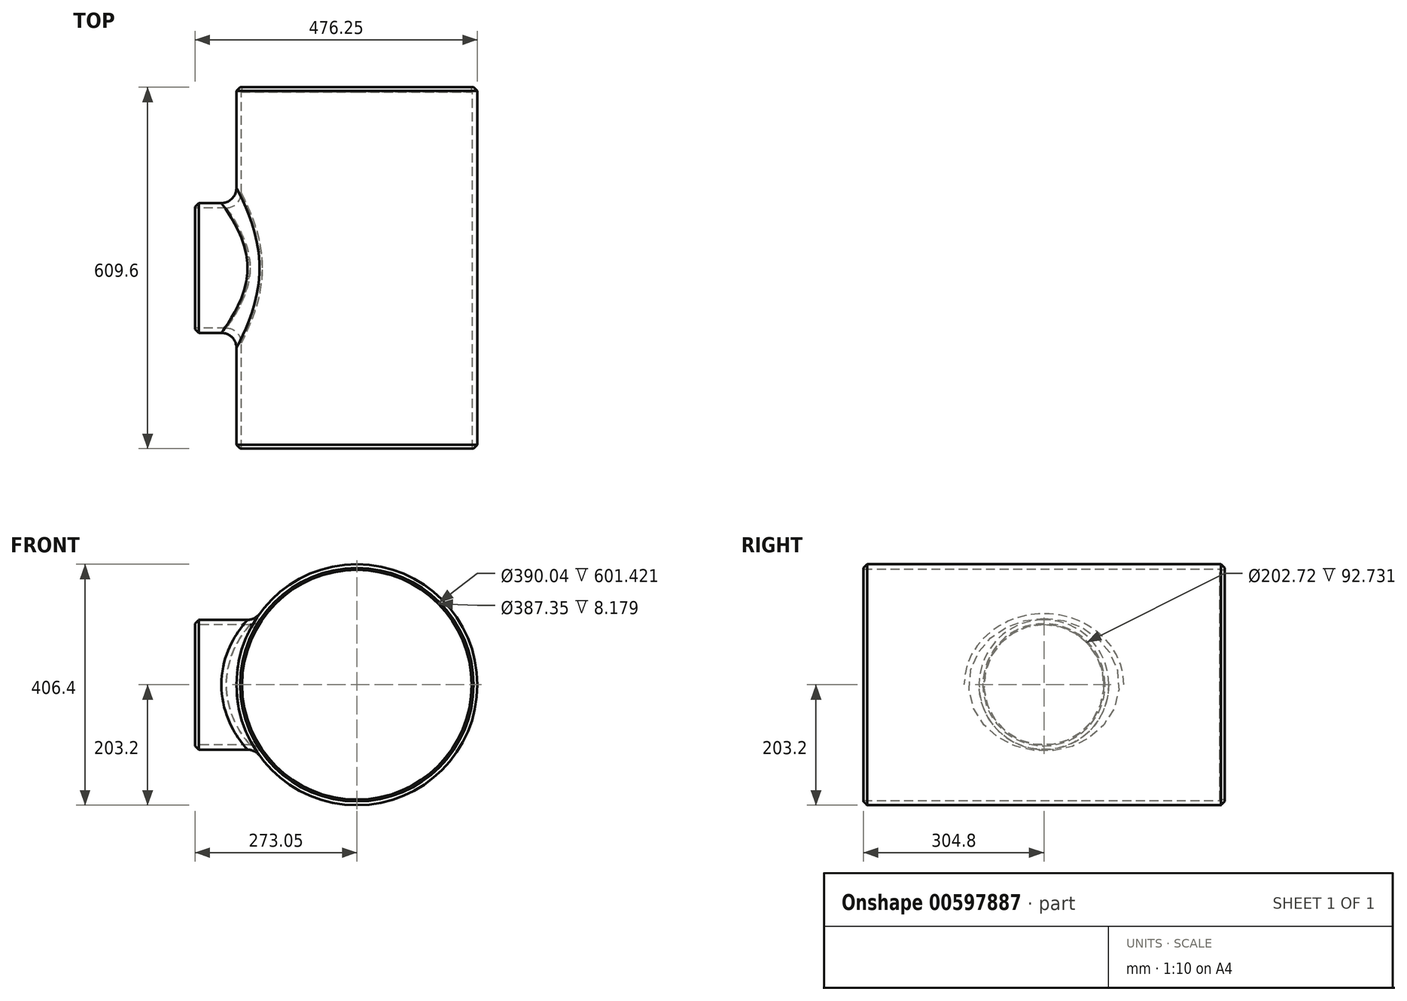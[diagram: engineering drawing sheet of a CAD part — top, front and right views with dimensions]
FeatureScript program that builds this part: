
annotation { "Feature Type Name" : "Feature", "Feature Type Description" : "" }
export const myFeature = defineFeature(function(context is Context, id is Id, definition is map)
    precondition{}
    {
        {
            var Q0;
            Q0=qCreatedBy(makeId("Top.planeOp"),FACE);
            var sketch = newSketch(context, id + "F0", { "sketchPlane" : qUnion([Q0])});
            skLineSegment(sketch, "E0.bottom", {"start": v(203.2, 304.8) * mm, "end": v(-203.2, 304.8) * mm});
            skLineSegment(sketch, "E0.top", {"start": v(203.2, -304.8) * mm, "end": v(-203.2, -304.8) * mm});
            skLineSegment(sketch, "E0.left", {"start": v(203.2, 304.8) * mm, "end": v(203.2, -304.8) * mm});
            skLineSegment(sketch, "E0.right", {"start": v(-203.2, 304.8) * mm, "end": v(-203.2, -304.8) * mm});
            skPoint(sketch, "E0.middle", {"position": v(0, 0) * mm});
            skSolve(sketch);
        }
        {
            var Q0;
            Q0 = qSketchRegion(id + "F0", true);
            extrude(context, id + "F1", {"entities" : qUnion([Q0]), "depth" : 406.4 * mm, "offsetDistance" : 25.4 * mm});
        }
        {
            var Q0;
            Q0=makeQuery(id+"F1.opExtrude","SWEPT_FACE",FACE,{"disambiguationData":[OSD([sQuery(id+"F0.wireOp",EDGE,"E0.right")])]});
            var sketch = newSketch(context, id + "F2", { "sketchPlane" : qUnion([Q0])});
            skCircle(sketch, "E1", {"center": v(0, 203.2) * mm, "radius": 109.47 * mm});
            skPoint(sketch, "E1.centerSnap0", {"position": v(304.8, 203.2) * mm});
            skSolve(sketch);
        }
        {
            var Q0;
            Q0 = qSketchRegion(id + "F2", true);
            extrude(context, id + "F3", {"entities" : qUnion([Q0]), "operationType" : NewBodyOperationType.ADD, "depth" : 69.85 * mm, "offsetDistance" : 25.4 * mm});
        }
        {
            var Q0;
            Q0=makeQuery(id+"F1.opExtrude","CAP_EDGE",EDGE,{"disambiguationData":[OSD([sQuery(id+"F0.wireOp",EDGE,"E0.left")])],"isStart":false});
            var Q1;
            Q1=makeQuery(id+"F1.opExtrude","CAP_EDGE",EDGE,{"disambiguationData":[OSD([sQuery(id+"F0.wireOp",EDGE,"E0.right")])],"isStart":false});
            var Q2;
            Q2=makeQuery(id+"F1.opExtrude","CAP_EDGE",EDGE,{"disambiguationData":[OSD([sQuery(id+"F0.wireOp",EDGE,"E0.right")])],"isStart":true});
            var Q3;
            Q3=makeQuery(id+"F1.opExtrude","CAP_EDGE",EDGE,{"disambiguationData":[OSD([sQuery(id+"F0.wireOp",EDGE,"E0.left")])],"isStart":true});
            fillet(context, id + "F4", {"entities" : qUnion([Q0, Q1, Q2, Q3]), "radius" : 203.2 * mm, "tangentPropagation" : true, "allowEdgeOverflow" : false});
        }
        {
            var Q0;
            Q0=makeQuery(id+"F1.opExtrude","SWEPT_FACE",FACE,{"disambiguationData":[OSD([sQuery(id+"F0.wireOp",EDGE,"E0.top")])]});
            shell(context, id + "F5", {"entities" : qUnion([Q0]), "thickness" : 8.18 * mm});
        }
        {
            var Q0;
            Q0=makeQuery(id+"F3.opExtrude","CAP_FACE",FACE,{"disambiguationData":[OSD([sQuery(id+"F2.wireOp",EDGE,"E1")])],"isStart":false});
            var sketch = newSketch(context, id + "F6", { "sketchPlane" : qUnion([Q0])});
            skCircle(sketch, "E2", {"center": v(0, 203.2) * mm, "radius": 101.36 * mm});
            skSolve(sketch);
        }
        {
            var Q0;
            Q0 = qSketchRegion(id + "F6", true);
            extrude(context, id + "F7", {"entities" : qUnion([Q0]), "operationType" : NewBodyOperationType.REMOVE, "oppositeDirection" : true, "depth" : 203.2 * mm, "offsetDistance" : 25.4 * mm});
        }
        {
            var Q0;
            Q0=makeQuery(id+"F4.opFillet","BLEND_EDGE",EDGE,{"blendedFrom":[makeQuery(id+"F1.opExtrude","CAP_EDGE",EDGE,{"disambiguationData":[OSD([sQuery(id+"F0.wireOp",EDGE,"E0.right")])],"isStart":false}),makeQuery(id+"F3.opExtrude","SWEPT_FACE",FACE,{"disambiguationData":[OSD([sQuery(id+"F2.wireOp",EDGE,"E1")])]})],"blendedInto":[makeQuery(id+"F3.opExtrude","SWEPT_FACE",FACE,{"disambiguationData":[OSD([sQuery(id+"F2.wireOp",EDGE,"E1")])]})]});
            var Q1;
            Q1=makeQuery(id+"F7.boolean.opBoolean","INTERSECT",EDGE,{"derivedFrom":[makeQuery(id+"F5.opShell","OFFSET_FACE",FACE,{"disambiguationData":[OSD([sQuery(id+"F0.wireOp",EDGE,"E0.left")])]}),makeQuery(id+"F7.opExtrude","SWEPT_FACE",FACE,{"disambiguationData":[OSD([sQuery(id+"F6.wireOp",EDGE,"E2")])]})]});
            fillet(context, id + "F8", {"entities" : qUnion([Q0, Q1]), "radius" : 25.4 * mm, "tangentPropagation" : true, "allowEdgeOverflow" : false});
        }
        {
            var Q0;
            Q0=makeQuery(id+"F4.opFillet","BLEND_EDGE",EDGE,{"blendedFrom":[makeQuery(id+"F1.opExtrude","CAP_EDGE",EDGE,{"disambiguationData":[OSD([sQuery(id+"F0.wireOp",EDGE,"E0.left")])],"isStart":true}),makeQuery(id+"F1.opExtrude","SWEPT_FACE",FACE,{"disambiguationData":[OSD([sQuery(id+"F0.wireOp",EDGE,"E0.top")])]})],"blendedInto":[makeQuery(id+"F1.opExtrude","SWEPT_FACE",FACE,{"disambiguationData":[OSD([sQuery(id+"F0.wireOp",EDGE,"E0.top")])]})]});
            var Q1;
            Q1=makeQuery(id+"F4.opFillet","BLEND_EDGE",EDGE,{"blendedFrom":[makeQuery(id+"F1.opExtrude","CAP_EDGE",EDGE,{"disambiguationData":[OSD([sQuery(id+"F0.wireOp",EDGE,"E0.left")])],"isStart":true}),makeQuery(id+"F1.opExtrude","SWEPT_FACE",FACE,{"disambiguationData":[OSD([sQuery(id+"F0.wireOp",EDGE,"E0.bottom")])]})],"blendedInto":[makeQuery(id+"F1.opExtrude","SWEPT_FACE",FACE,{"disambiguationData":[OSD([sQuery(id+"F0.wireOp",EDGE,"E0.bottom")])]})]});
            var Q2;
            Q2=makeQuery(id+"F3.opExtrude","CAP_EDGE",EDGE,{"disambiguationData":[OSD([sQuery(id+"F2.wireOp",EDGE,"E1")])],"isStart":false});
            chamfer(context, id + "F9", {"entities" : qUnion([Q0, Q1, Q2]), "width" : 6.35 * mm, "tangentPropagation" : true});
        }
        {
            var Q0;
            Q0=makeQuery(id+"F1.opExtrude","SWEPT_FACE",FACE,{"disambiguationData":[OSD([sQuery(id+"F0.wireOp",EDGE,"E0.bottom")])]});
            var sketch = newSketch(context, id + "F10", { "sketchPlane" : qUnion([Q0])});
            skCircle(sketch, "E3", {"center": v(0, 203.2) * mm, "radius": 193.68 * mm});
            skSolve(sketch);
        }
        {
            var Q0;
            Q0 = qSketchRegion(id + "F10", true);
            extrude(context, id + "F11", {"entities" : qUnion([Q0]), "operationType" : NewBodyOperationType.REMOVE, "endBound" : BoundingType.THROUGH_ALL, "oppositeDirection" : true, "depth" : 25.4 * mm, "offsetDistance" : 25.4 * mm});
        }
    });
